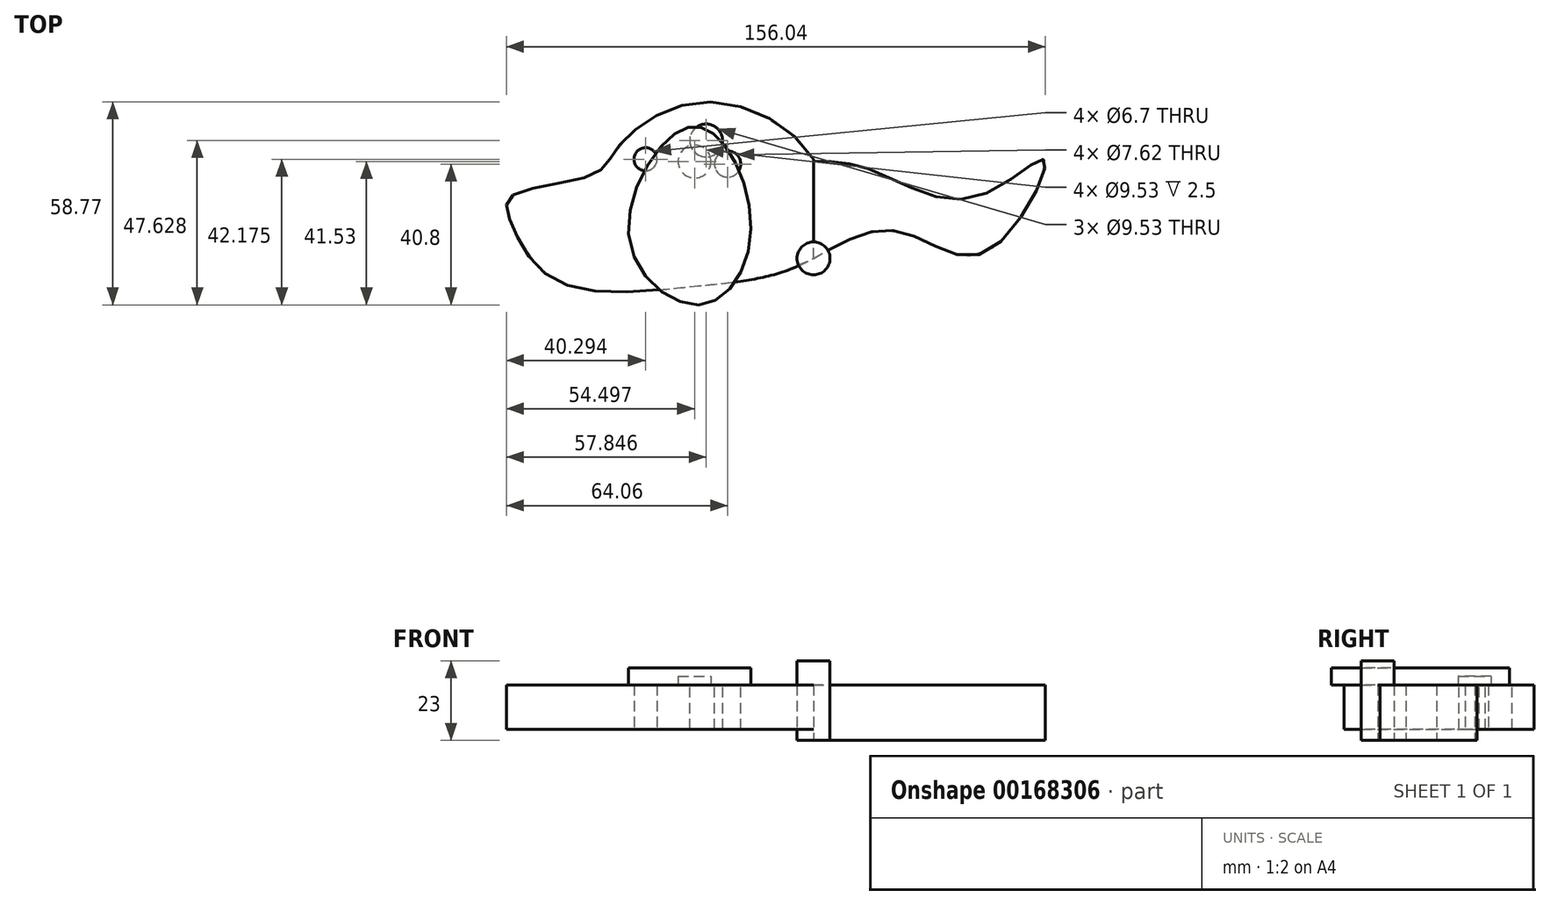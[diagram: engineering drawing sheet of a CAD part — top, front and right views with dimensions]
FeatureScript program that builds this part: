
annotation { "Feature Type Name" : "Feature", "Feature Type Description" : "" }
export const myFeature = defineFeature(function(context is Context, id is Id, definition is map)
    precondition{}
    {
        {
            var Q0;
            Q0=qCreatedBy(makeId("Top.planeOp"),FACE);
            var sketch = newSketch(context, id + "F0", { "sketchPlane" : qUnion([Q0])});
            skLineSegment(sketch, "E0", {"start": v(0, 0) * mm, "end": v(0, 35.75) * mm});
            skFitSpline(sketch, "E1", {"points": [v(0, 35.75) * mm, v(-42.29, 56.4) * mm, v(-71.14, 39.72) * mm, v(-79.96, 30.28) * mm, v(-109.5, 22.4) * mm, v(-109.57, 13.36) * mm, v(-92.92, -8.18) * mm, v(-41.84, -9.95) * mm, v(0, 0) * mm], "startDerivative": vector(-150.52, 258.32) * mm, "endDerivative": vector(283.65, 155.96) * mm});
            skSolve(sketch);
        }
        {
            var Q0;
            Q0=makeQuery(id+"F0.imprint","IMPRINT",FACE,{"disambiguationData":[TD([[makeQuery(id+"F0.imprint","IMPRINT",EDGE,{"derivedFrom":sQuery(id+"F0.wireOp",EDGE,"E0")}),1.0]])]});
            extrude(context, id + "F1", {"entities" : qUnion([Q0]), "depth" : 16 * mm});
        }
        {
            var Q0;
            Q0=qCreatedBy(makeId("Top.planeOp"),FACE);
            var sketch = newSketch(context, id + "F2", { "sketchPlane" : qUnion([Q0])});
            skCircle(sketch, "E2", {"center": v(-60.78, 35.86) * mm, "radius": 4.19 * mm});
            skSolve(sketch);
        }
        {
            var Q0;
            Q0 = qSketchRegion(id + "F2", true);
            var Q1;
            Q1 = qConstructionFilter(qBodyType(qCreatedBy(id + "F2" ,EDGE), BodyType.WIRE), ConstructionObject.NO);
            extrude(context, id + "F3", {"entities" : qUnion([Q0]), "operationType" : NewBodyOperationType.REMOVE, "surfaceEntities" : qUnion([Q1]), "depth" : 25 * mm});
        }
        {
            var Q0;
            Q0=makeQuery(id+"F1.opExtrude","CAP_FACE",FACE,{"disambiguationData":[OSD([sQuery(id+"F0.wireOp",EDGE,"E0"),sQuery(id+"F0.wireOp",EDGE,"E1")])],"isStart":false});
            var sketch = newSketch(context, id + "F4", { "sketchPlane" : qUnion([Q0])});
            skFitSpline(sketch, "E3", {"points": [v(-40.18, 36.07) * mm, v(-53.16, 4.5) * mm, v(-32.24, -13.4) * mm, v(-18.17, 7.22) * mm, v(-28.54, 35.7) * mm, v(-40.18, 36.07) * mm]});
            skSolve(sketch);
        }
        {
            var Q0;
            Q0 = qSketchRegion(id + "F4", true);
            extrude(context, id + "F5", {"entities" : qUnion([Q0]), "depth" : 5 * mm});
        }
        {
            var Q0;
            Q0=makeQuery(id+"F5.opExtrude","CAP_FACE",FACE,{"disambiguationData":[OSD([sQuery(id+"F4.wireOp",EDGE,"E3")])],"isStart":true});
            var sketch = newSketch(context, id + "F6", { "sketchPlane" : qUnion([Q0])});
            skCircle(sketch, "E4", {"center": v(-34.42, -28.04) * mm, "radius": 4.76 * mm});
            skSolve(sketch);
        }
        {
            var Q0;
            Q0 = qSketchRegion(id + "F6", true);
            extrude(context, id + "F7", {"entities" : qUnion([Q0]), "operationType" : NewBodyOperationType.REMOVE, "oppositeDirection" : true, "depth" : 2.5 * mm});
        }
        {
            var Q0;
            Q0=qCreatedBy(makeId("Top.planeOp"),FACE);
            var sketch = newSketch(context, id + "F8", { "sketchPlane" : qUnion([Q0])});
            skCircle(sketch, "E5", {"center": v(0, 0) * mm, "radius": 4.76 * mm});
            skSolve(sketch);
        }
        {
            var Q0;
            Q0=makeQuery(id+"F8.imprint","IMPRINT",FACE,{"disambiguationData":[TD([[makeQuery(id+"F8.imprint","IMPRINT",EDGE,{"derivedFrom":sQuery(id+"F8.wireOp",EDGE,"E5")}),1.0]])]});
            extrude(context, id + "F9", {"entities" : qUnion([Q0]), "depth" : 23 * mm});
        }
        {
            var Q0;
            Q0=makeQuery(id+"F1.opExtrude","CAP_FACE",FACE,{"disambiguationData":[OSD([sQuery(id+"F0.wireOp",EDGE,"E0"),sQuery(id+"F0.wireOp",EDGE,"E1")])],"isStart":false});
            var sketch = newSketch(context, id + "F10", { "sketchPlane" : qUnion([Q0])});
            skCircle(sketch, "E6", {"center": v(-31.07, 34.14) * mm, "radius": 4.76 * mm});
            skSolve(sketch);
        }
        {
            var Q0;
            Q0=makeQuery(id+"F10.imprint","IMPRINT",FACE,{"disambiguationData":[TD([[makeQuery(id+"F10.imprint","IMPRINT",EDGE,{"derivedFrom":sQuery(id+"F10.wireOp",EDGE,"E6")}),1.0]])]});
            extrude(context, id + "F11", {"entities" : qUnion([Q0]), "operationType" : NewBodyOperationType.REMOVE, "oppositeDirection" : true, "depth" : 25 * mm});
        }
        {
            var Q0;
            Q0=makeQuery(id+"F1.opExtrude","SWEPT_BODY",BODY,{"disambiguationData":[OSD([sQuery(id+"F0.wireOp",EDGE,"E0"),sQuery(id+"F0.wireOp",EDGE,"E1")])]});
            var Q1;
            {var subQ0=sQuery(id+"F0.wireOp",EDGE,"E1");var subQ1=sQuery(id+"F0.wireOp",EDGE,"E0");Q1=makeQuery(id+"F1.opExtrude","CAP_VERTEX",VERTEX,{"disambiguationData":[OSD([subQ1,subQ0]),TDD([makeQuery(id+"F0.imprint","INTERSECT",VERTEX,{"disambiguationData":[OD(0.0)],"derivedFrom":[subQ1,subQ0]})])],"isStart":false});}
            transform(context, id + "F12", {"entities" : qUnion([Q0]), "transformType" : TransformType.SCALE_UNIFORMLY, "scale" : .8, "scalePoint" : qUnion([Q1]), "makeCopy" : true});
        }
        {
            var Q0;
            Q0=makeQuery(id+"F1.opExtrude","SWEPT_BODY",BODY,{"disambiguationData":[OSD([sQuery(id+"F0.wireOp",EDGE,"E0"),sQuery(id+"F0.wireOp",EDGE,"E1")])]});
            var Q1;
            {var subQ0=sQuery(id+"F0.wireOp",EDGE,"E1");var subQ1=sQuery(id+"F0.wireOp",EDGE,"E0");Q1=makeQuery(id+"F1.opExtrude","CAP_VERTEX",VERTEX,{"disambiguationData":[OSD([subQ1,subQ0]),TDD([makeQuery(id+"F0.imprint","INTERSECT",VERTEX,{"disambiguationData":[OD(0.0)],"derivedFrom":[subQ1,subQ0]})])],"isStart":false});}
            transform(context, id + "F13", {"entities" : qUnion([Q0]), "transformType" : TransformType.SCALE_UNIFORMLY, "scale" : .8, "scalePoint" : qUnion([Q1]), "makeCopy" : false});
        }
        {
            var Q0;
            Q0=qCreatedBy(makeId("Top.planeOp"),FACE);
            var sketch = newSketch(context, id + "F14", { "sketchPlane" : qUnion([Q0])});
            skLineSegment(sketch, "E7", {"start": v(0, 0) * mm, "end": v(0, 28.13) * mm});
            skFitSpline(sketch, "E8", {"points": [v(0, 0) * mm, v(25.24, 7.75) * mm, v(49.9, 1.79) * mm, v(66.93, 28.42) * mm, v(47.16, 17.79) * mm, v(17.44, 25.31) * mm, v(0, 28.13) * mm], "startDerivative": vector(158.01, 89.24) * mm, "endDerivative": vector(-120.2, -3.25) * mm});
            skSolve(sketch);
        }
        {
            var Q0;
            Q0=makeQuery(id+"F14.imprint","IMPRINT",FACE,{"disambiguationData":[TD([[makeQuery(id+"F14.imprint","IMPRINT",EDGE,{"derivedFrom":sQuery(id+"F14.wireOp",EDGE,"E7")}),-1.0]])]});
            extrude(context, id + "F15", {"entities" : qUnion([Q0]), "depth" : 16 * mm});
        }
        {
            var Q0;
            Q0=makeQuery(id+"F12.opPattern","COPY",BODY,{"derivedFrom":makeQuery(id+"F1.opExtrude","SWEPT_BODY",BODY,{"disambiguationData":[OSD([sQuery(id+"F0.wireOp",EDGE,"E0"),sQuery(id+"F0.wireOp",EDGE,"E1")])]}),"instanceName":"1"});
            deleteBodies(context, id + "F16", {"entities" : qUnion([Q0])});
        }
    });
